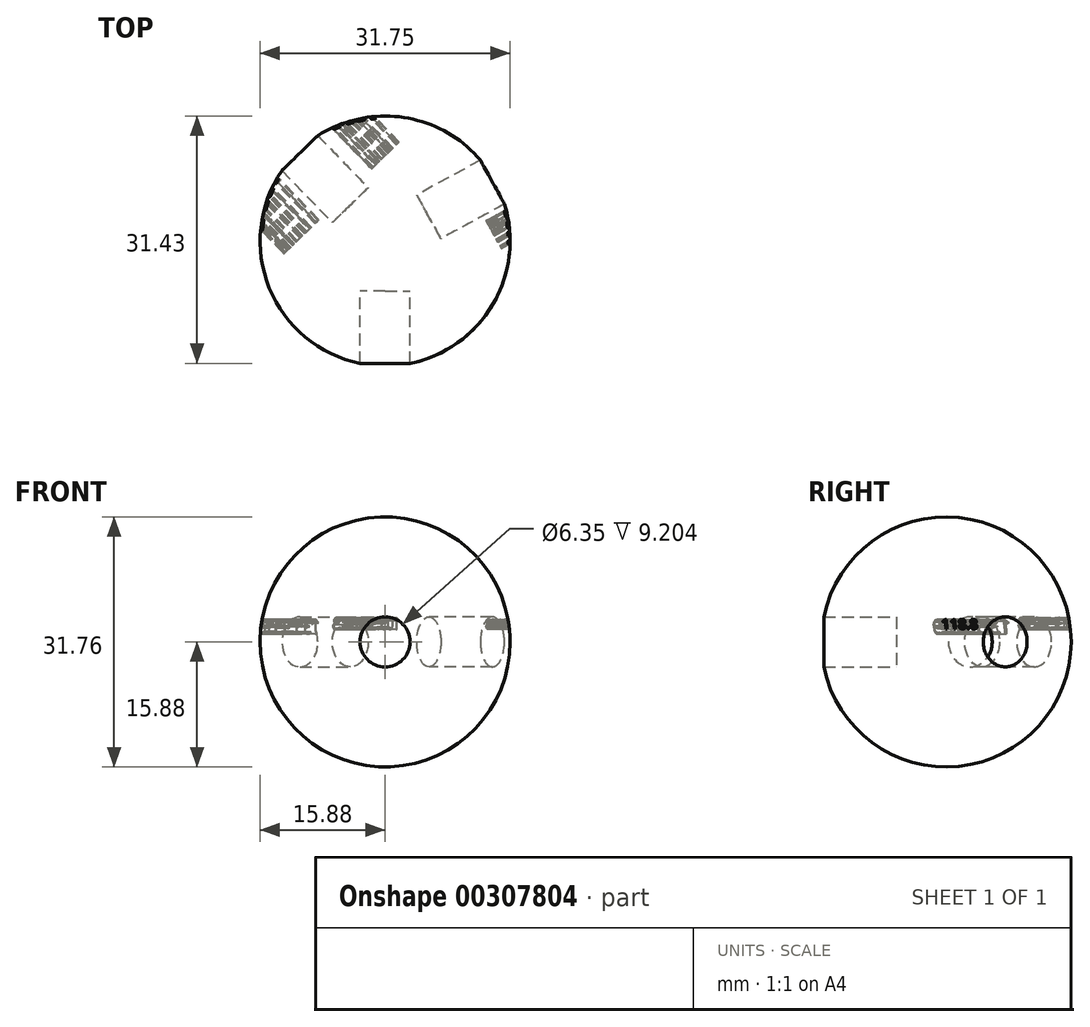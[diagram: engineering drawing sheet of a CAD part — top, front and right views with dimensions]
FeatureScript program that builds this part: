
annotation { "Feature Type Name" : "Feature", "Feature Type Description" : "" }
export const myFeature = defineFeature(function(context is Context, id is Id, definition is map)
    precondition{}
    {
        {
            var Q0;
            Q0=qCreatedBy(makeId("Top.planeOp"),FACE);
            var sketch = newSketch(context, id + "F0", { "sketchPlane" : qUnion([Q0])});
            skArc(sketch, "E0", {"start": v(0, 15.88) * mm, "mid": v(-15.88, 0) * mm, "end": v(0, -15.88) * mm});
            skLineSegment(sketch, "E1", {"start": v(0, 15.88) * mm, "end": v(0, -15.88) * mm});
            skSolve(sketch);
        }
        {
            var Q0;
            Q0=makeQuery(id+"F0.imprint","IMPRINT",FACE,{"disambiguationData":[TD([[makeQuery(id+"F0.imprint","IMPRINT",EDGE,{"derivedFrom":sQuery(id+"F0.wireOp",EDGE,"E0")}),1.0]])]});
            var Q1;
            Q1=sQuery(id+"F0.wireOp",EDGE,"E1");
            revolve(context, id + "F1", {"entities" : qUnion([Q0]), "axis" : qUnion([Q1]), "revolveType" : RevolveType.FULL});
        }
        {
            var Q0;
            Q0=qCreatedBy(makeId("Front.planeOp"),FACE);
            var sketch = newSketch(context, id + "F2", { "sketchPlane" : qUnion([Q0])});
            skLineSegment(sketch, "E2", {"start": v(0, 0) * mm, "end": v(0, 73.36) * mm, "construction": true});
            skSolve(sketch);
        }
        {
            var Q0;
            Q0=qCreatedBy(makeId("Front.planeOp"),FACE);
            cPlane(context, id + "F3", {"entities" : qUnion([Q0]), "cplaneType" : CPlaneType.OFFSET, "offset" : 6.35 * mm, "width" : 152.4 * mm, "height" : 152.4 * mm});
        }
        {
            var Q0;
            Q0=qCreatedBy(id+"F3.planeOp",FACE);
            var sketch = newSketch(context, id + "F4", { "sketchPlane" : qUnion([Q0])});
            skCircle(sketch, "E3", {"center": v(0, 0) * mm, "radius": 3.18 * mm});
            skSolve(sketch);
        }
        {
            var Q0;
            Q0 = qSketchRegion(id + "F4", true);
            extrude(context, id + "F5", {"entities" : qUnion([Q0]), "depth" : 25.4 * mm});
        }
        {
            var Q0;
            Q0=makeQuery(id+"F5.opExtrude","SWEPT_BODY",BODY,{"disambiguationData":[OSD([sQuery(id+"F4.wireOp",EDGE,"E3")])]});
            var Q1;
            Q1=sQuery(id+"F2.wireOp",EDGE,"E2");
            var Q2;
            Q2=sQuery(id+"F2.wireOp",EDGE,"E2");
            transform(context, id + "F6", {"entities" : qUnion([Q0]), "transformType" : TransformType.ROTATION, "transformAxis" : qUnion([Q2]), "angle" : 135.9 * degree, "oppositeDirection" : true, "makeCopy" : true});
        }
        {
            var Q0;
            Q0=makeQuery(id+"F6.opPattern","COPY",BODY,{"derivedFrom":makeQuery(id+"F5.opExtrude","SWEPT_BODY",BODY,{"disambiguationData":[OSD([sQuery(id+"F4.wireOp",EDGE,"E3")])]}),"instanceName":"1"});
            var Q1;
            Q1=sQuery(id+"F2.wireOp",EDGE,"E2");
            transform(context, id + "F7", {"entities" : qUnion([Q0]), "transformType" : TransformType.ROTATION, "transformAxis" : qUnion([Q1]), "angle" : 105.3 * degree, "oppositeDirection" : true, "makeCopy" : true});
        }
        {
            var Q0;
            Q0=makeQuery(id+"F5.opExtrude","SWEPT_BODY",BODY,{"disambiguationData":[OSD([sQuery(id+"F4.wireOp",EDGE,"E3")])]});
            var Q1;
            Q1=makeQuery(id+"F6.opPattern","COPY",BODY,{"derivedFrom":makeQuery(id+"F5.opExtrude","SWEPT_BODY",BODY,{"disambiguationData":[OSD([sQuery(id+"F4.wireOp",EDGE,"E3")])]}),"instanceName":"1"});
            var Q2;
            Q2=makeQuery(id+"F7.opPattern","COPY",BODY,{"derivedFrom":makeQuery(id+"F6.opPattern","COPY",BODY,{"derivedFrom":makeQuery(id+"F5.opExtrude","SWEPT_BODY",BODY,{"disambiguationData":[OSD([sQuery(id+"F4.wireOp",EDGE,"E3")])]}),"instanceName":"1"}),"instanceName":"1"});
            var Q3;
            Q3=makeQuery(id+"F1.opRevolve","SWEPT_BODY",BODY,{"disambiguationData":[OSD([sQuery(id+"F0.wireOp",EDGE,"E0"),sQuery(id+"F0.wireOp",EDGE,"E1")])]});
            booleanBodies(context, id + "F8", {"operationType" : BooleanOperationType.SUBTRACTION, "tools" : qUnion([Q0, Q1, Q2]), "targets" : qUnion([Q3])});
        }
        {
            var Q0;
            Q0=makeQuery(id+"F8.opBoolean","COPY",FACE,{"derivedFrom":makeQuery(id+"F6.opPattern","COPY",FACE,{"derivedFrom":makeQuery(id+"F5.opExtrude","CAP_FACE",FACE,{"disambiguationData":[OSD([sQuery(id+"F4.wireOp",EDGE,"E3")])],"isStart":true}),"instanceName":"1"})});
            cPlane(context, id + "F9", {"entities" : qUnion([Q0]), "cplaneType" : CPlaneType.OFFSET, "offset" : 12.47 * mm, "width" : 152.4 * mm, "height" : 152.4 * mm});
        }
        {
            var Q0;
            Q0=qCreatedBy(id+"F9.planeOp",FACE);
            var sketch = newSketch(context, id + "F10", { "sketchPlane" : qUnion([Q0])});
            skText(sketch, "E4", { "text": "105.3", "fontName": "OpenSans-Regular.ttf"});
            skText(sketch, "E5", { "text": "135.9", "fontName": "OpenSans-Regular.ttf"});
            const initialGuessF10  = {"E4": [-0.01023, 0.0016, 1, 0, 0.00147], "E5": [0.00394, 0.00102, 1, 0, 0.00185]};
            skSetInitialGuess(sketch, initialGuessF10);
            skSolve(sketch);
        }
        {
            var Q0;
            Q0 = qSketchRegion(id + "F10", true);
            extrude(context, id + "F11", {"entities" : qUnion([Q0]), "operationType" : NewBodyOperationType.REMOVE, "oppositeDirection" : true, "depth" : 11.02 * mm});
        }
        {
            var Q0;
            Q0=makeQuery(id+"F8.opBoolean","COPY",FACE,{"derivedFrom":makeQuery(id+"F7.opPattern","COPY",FACE,{"derivedFrom":makeQuery(id+"F6.opPattern","COPY",FACE,{"derivedFrom":makeQuery(id+"F5.opExtrude","CAP_FACE",FACE,{"disambiguationData":[OSD([sQuery(id+"F4.wireOp",EDGE,"E3")])],"isStart":true}),"instanceName":"1"}),"instanceName":"1"})});
            cPlane(context, id + "F12", {"entities" : qUnion([Q0]), "cplaneType" : CPlaneType.OFFSET, "offset" : 12.5 * mm, "width" : 152.4 * mm, "height" : 152.4 * mm});
        }
        {
            var Q0;
            Q0=qCreatedBy(id+"F12.planeOp",FACE);
            var sketch = newSketch(context, id + "F13", { "sketchPlane" : qUnion([Q0])});
            skText(sketch, "E6", { "text": "118.8", "fontName": "OpenSans-Regular.ttf"});
            const initialGuessF13  = {"E6": [-0.0081, 0.00167, 1, 0, 0.0012]};
            skSetInitialGuess(sketch, initialGuessF13);
            skSolve(sketch);
        }
        {
            var Q0;
            Q0 = qSketchRegion(id + "F13", true);
            extrude(context, id + "F14", {"entities" : qUnion([Q0]), "operationType" : NewBodyOperationType.REMOVE, "oppositeDirection" : true, "depth" : 6.35 * mm});
        }
    });
